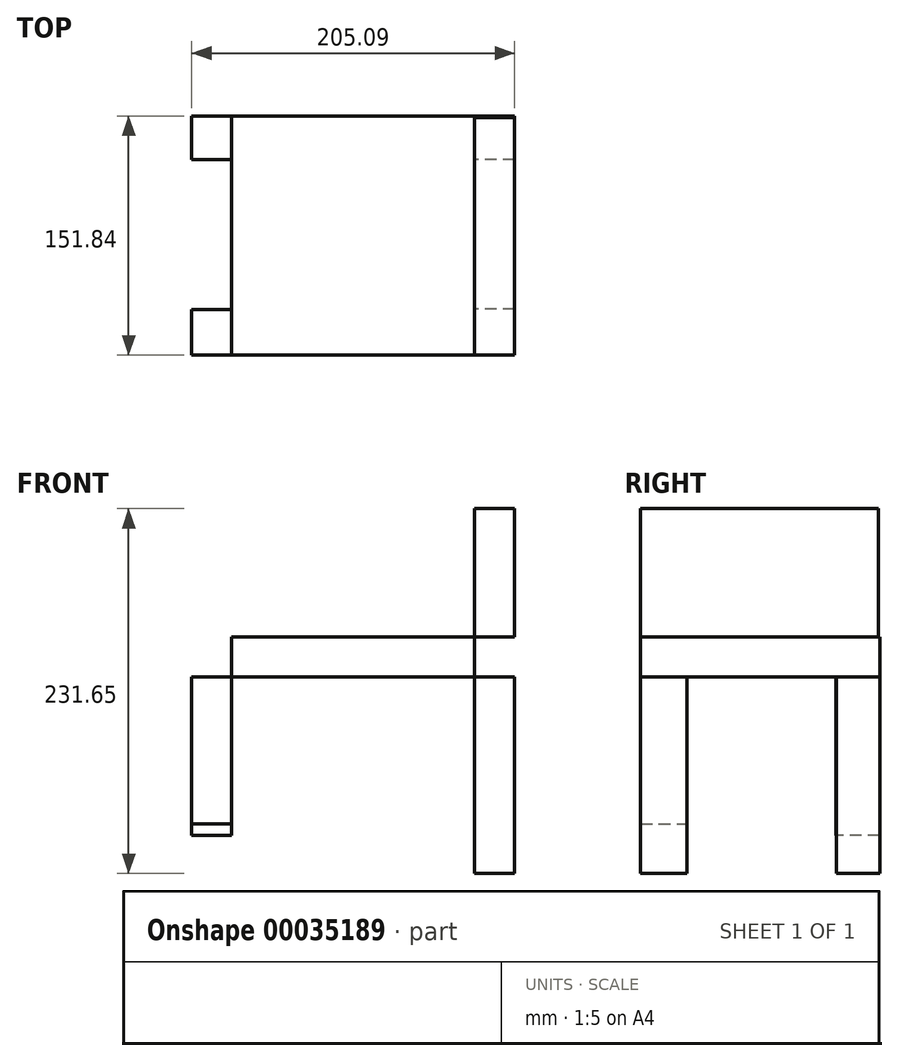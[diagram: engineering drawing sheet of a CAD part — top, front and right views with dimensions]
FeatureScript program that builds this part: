
annotation { "Feature Type Name" : "Feature", "Feature Type Description" : "" }
export const myFeature = defineFeature(function(context is Context, id is Id, definition is map)
    precondition{}
    {
        {
            var Q0;
            Q0=qCreatedBy(makeId("Top.planeOp"),FACE);
            var sketch = newSketch(context, id + "F0", { "sketchPlane" : qUnion([Q0])});
            skLineSegment(sketch, "E0.bottom", {"start": v(-75.98, 77.13) * mm, "end": v(78.31, 77.13) * mm});
            skLineSegment(sketch, "E0.top", {"start": v(-75.98, -74.71) * mm, "end": v(78.31, -74.71) * mm});
            skLineSegment(sketch, "E0.left", {"start": v(-75.98, 77.13) * mm, "end": v(-75.98, -74.71) * mm});
            skLineSegment(sketch, "E0.right", {"start": v(78.31, 77.13) * mm, "end": v(78.31, -74.71) * mm});
            skSolve(sketch);
        }
        {
            var Q0;
            Q0 = qSketchRegion(id + "F0", true);
            extrude(context, id + "F1", {"entities" : qUnion([Q0]), "depth" : 25.4 * mm});
        }
        {
            var Q0;
            Q0=makeQuery(id+"F1.opExtrude","SWEPT_FACE",FACE,{"disambiguationData":[OSD([sQuery(id+"F0.wireOp",EDGE,"E0.right")])]});
            var sketch = newSketch(context, id + "F2", { "sketchPlane" : qUnion([Q0])});
            skLineSegment(sketch, "E1.bottom", {"start": v(-74.71, 25.4) * mm, "end": v(76.25, 25.4) * mm});
            skLineSegment(sketch, "E1.top", {"start": v(-74.71, 106.88) * mm, "end": v(76.25, 106.88) * mm});
            skLineSegment(sketch, "E1.left", {"start": v(-74.71, 25.4) * mm, "end": v(-74.71, 106.88) * mm});
            skLineSegment(sketch, "E1.right", {"start": v(76.25, 25.4) * mm, "end": v(76.25, 106.88) * mm});
            skSolve(sketch);
        }
        {
            var Q0;
            Q0 = qSketchRegion(id + "F2", true);
            extrude(context, id + "F3", {"entities" : qUnion([Q0]), "depth" : 25.4 * mm});
        }
        {
            var Q0;
            Q0=makeQuery(id+"F1.opExtrude","SWEPT_FACE",FACE,{"disambiguationData":[OSD([sQuery(id+"F0.wireOp",EDGE,"E0.left")])]});
            var sketch = newSketch(context, id + "F4", { "sketchPlane" : qUnion([Q0])});
            skLineSegment(sketch, "E2.bottom", {"start": v(74.71, 0) * mm, "end": v(45.65, 0) * mm});
            skLineSegment(sketch, "E2.top", {"start": v(74.71, -93.24) * mm, "end": v(45.65, -93.24) * mm});
            skLineSegment(sketch, "E2.left", {"start": v(74.71, 0) * mm, "end": v(74.71, -93.24) * mm});
            skLineSegment(sketch, "E2.right", {"start": v(45.65, 0) * mm, "end": v(45.65, -93.24) * mm});
            skSolve(sketch);
        }
        {
            var Q0;
            Q0 = qSketchRegion(id + "F4", true);
            extrude(context, id + "F5", {"entities" : qUnion([Q0]), "depth" : 25.4 * mm});
        }
        {
            var Q0;
            Q0=makeQuery(id+"F1.opExtrude","SWEPT_FACE",FACE,{"disambiguationData":[OSD([sQuery(id+"F0.wireOp",EDGE,"E0.left")])]});
            var sketch = newSketch(context, id + "F6", { "sketchPlane" : qUnion([Q0])});
            skLineSegment(sketch, "E3.bottom", {"start": v(-77.13, 0) * mm, "end": v(-49.44, 0) * mm});
            skLineSegment(sketch, "E3.top", {"start": v(-77.13, -100.68) * mm, "end": v(-49.44, -100.68) * mm});
            skLineSegment(sketch, "E3.left", {"start": v(-77.13, 0) * mm, "end": v(-77.13, -100.68) * mm});
            skLineSegment(sketch, "E3.right", {"start": v(-49.44, 0) * mm, "end": v(-49.44, -100.68) * mm});
            skSolve(sketch);
        }
        {
            var Q0;
            Q0 = qSketchRegion(id + "F6", true);
            extrude(context, id + "F7", {"entities" : qUnion([Q0]), "depth" : 25.4 * mm});
        }
        {
            var Q0;
            Q0=makeQuery(id+"F1.opExtrude","SWEPT_FACE",FACE,{"disambiguationData":[OSD([sQuery(id+"F0.wireOp",EDGE,"E0.right")])]});
            var sketch = newSketch(context, id + "F8", { "sketchPlane" : qUnion([Q0])});
            skLineSegment(sketch, "E4.bottom", {"start": v(77.13, 0) * mm, "end": v(49.67, 0) * mm});
            skLineSegment(sketch, "E4.top", {"start": v(77.13, -124.77) * mm, "end": v(49.67, -124.77) * mm});
            skLineSegment(sketch, "E4.left", {"start": v(77.13, 0) * mm, "end": v(77.13, -124.77) * mm});
            skLineSegment(sketch, "E4.right", {"start": v(49.67, 0) * mm, "end": v(49.67, -124.77) * mm});
            skLineSegment(sketch, "E5.bottom", {"start": v(-74.71, 0) * mm, "end": v(-45.43, 0) * mm});
            skLineSegment(sketch, "E5.top", {"start": v(-74.71, -124.77) * mm, "end": v(-45.43, -124.77) * mm});
            skLineSegment(sketch, "E5.left", {"start": v(-74.71, 0) * mm, "end": v(-74.71, -124.77) * mm});
            skLineSegment(sketch, "E5.right", {"start": v(-45.43, 0) * mm, "end": v(-45.43, -124.77) * mm});
            skSolve(sketch);
        }
        {
            var Q0;
            Q0 = qSketchRegion(id + "F8", true);
            extrude(context, id + "F9", {"entities" : qUnion([Q0]), "depth" : 25.4 * mm});
        }
    });
